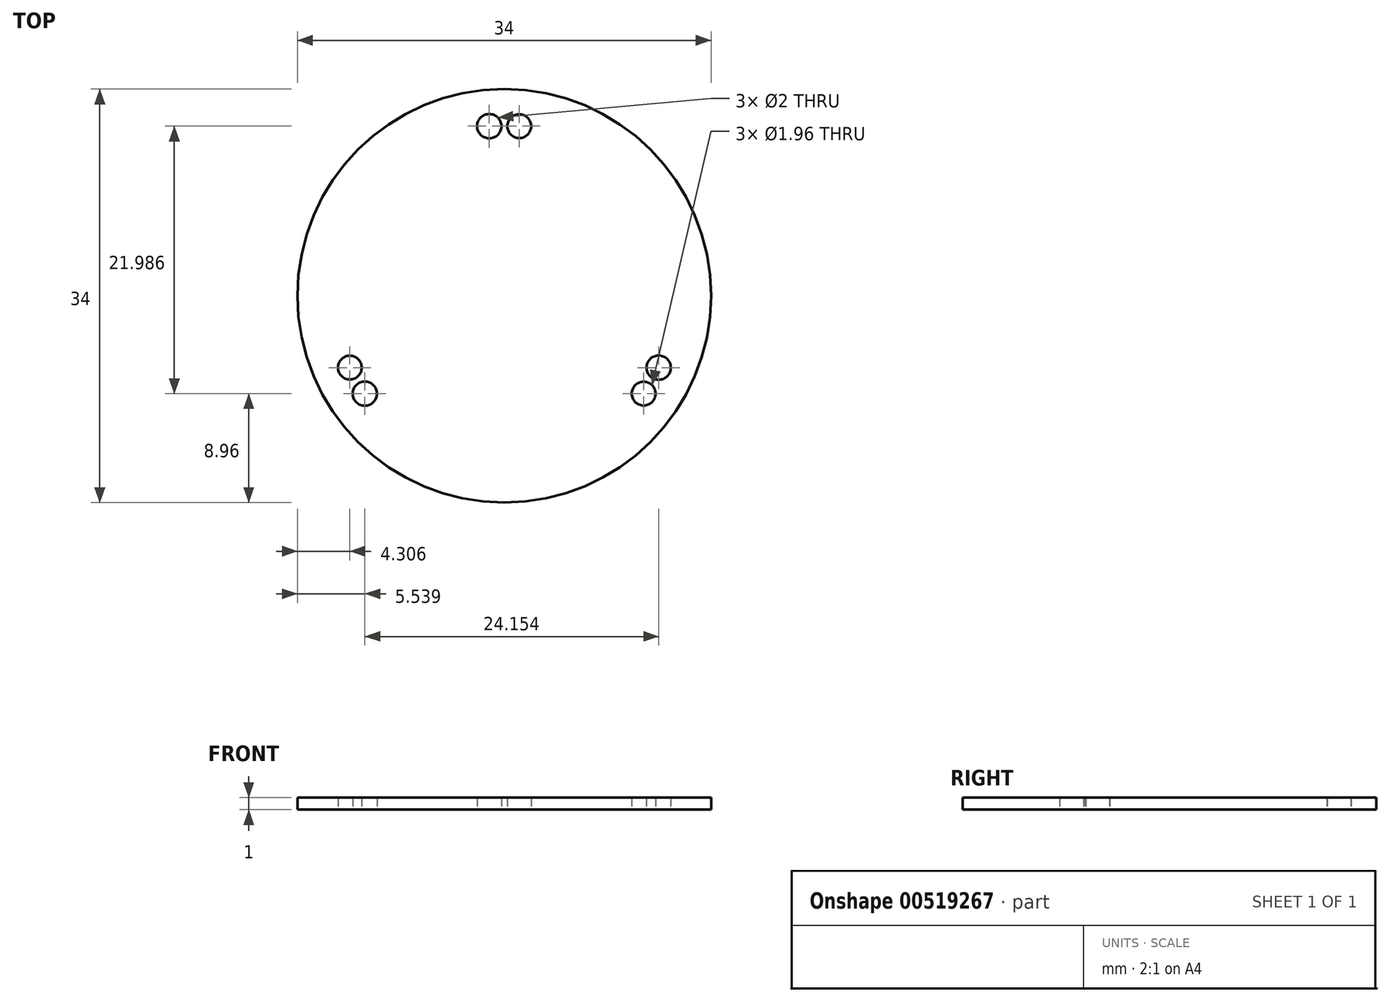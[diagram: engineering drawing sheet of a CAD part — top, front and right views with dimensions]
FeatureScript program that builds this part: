
annotation { "Feature Type Name" : "Feature", "Feature Type Description" : "" }
export const myFeature = defineFeature(function(context is Context, id is Id, definition is map)
    precondition{}
    {
        {
            var Q0;
            Q0=qCreatedBy(makeId("Top.planeOp"),FACE);
            var sketch = newSketch(context, id + "F0", { "sketchPlane" : qUnion([Q0])});
            skCircle(sketch, "E0", {"center": v(0, 0) * mm, "radius": 17 * mm});
            skCircle(sketch, "E1", {"center": v(-1.23, 13.95) * mm, "radius": 1 * mm});
            skCircle(sketch, "E2", {"center": v(0, 0) * mm, "radius": 14 * mm, "construction": true});
            skCircle(sketch, "E3", {"center": v(1.23, 13.95) * mm, "radius": 0.98 * mm});
            skCircle(sketch, "E4.1.0", {"center": v(-11.46, -8.04) * mm, "radius": 1 * mm});
            skCircle(sketch, "E4.2.0", {"center": v(12.7, -5.9) * mm, "radius": 1 * mm});
            skCircle(sketch, "E5.1.0", {"center": v(-12.7, -5.9) * mm, "radius": 0.98 * mm});
            skCircle(sketch, "E5.2.0", {"center": v(11.46, -8.04) * mm, "radius": 0.98 * mm});
            skSolve(sketch);
        }
        {
            var Q0;
            Q0=makeQuery(id+"F0.imprint","IMPRINT",FACE,{"disambiguationData":[TD([[makeQuery(id+"F0.imprint","IMPRINT",EDGE,{"derivedFrom":sQuery(id+"F0.wireOp",EDGE,"E0")}),1.0]])]});
            extrude(context, id + "F1", {"entities" : qUnion([Q0]), "depth" : 1 * mm, "offsetDistance" : 25 * mm});
        }
    });
